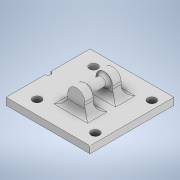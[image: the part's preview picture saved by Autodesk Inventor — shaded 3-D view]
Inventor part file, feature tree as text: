
AUTODESK INVENTOR PART (.ipt)
format: ipt  version: 2022 (Build 260153000, 153)  size: 207,360 bytes
history: native  units: in
note: dims shown in document units (in); Inventor stores cm internally (conversion verified against a paired STEP export)
features: sketch x6, extrude x4, fillet x3, hole x1
ambient origin geometry x8: Origin, YZ Plane, XZ Plane, XY Plane, X Axis, Y Axis, Z Axis, Center Point
bodies: Solid1 (feature_tree)
feature tree (14):
  extrude  "Extrusion1"  Depth=1.1811in
  hole  "Hole1"  [1 undecoded]
  extrude  "Extrusion2"  Depth=0.7953in
  extrude  "Extrusion3"  Depth=0.1929in
  fillet  "Fillet1"  Radius=0.7953in
  extrude  "Extrusion4"  Depth=0.0787in
  fillet  "Fillet2"  Radius=0.1929in
  fillet  "Fillet3"  Radius=0.1929in
  sketch  "Sketch6"  dims[d18=0.1181in d19=0.8189in d20=0.1929in d21=0.1929in d22=0.2362in d23=0.1181in d24=0.3346in d25=0.4094in d26=0.1181in d27=0.2756in d28=0.5354in d29=0.4094in d30=0.2756in d31=0.0in d32=0.1181in d33=0.1181in d34=0.1772in d35=0.1181in d36=0.1969in d37=0.0in d38=0.0394in d39=0.0787in]
  sketch  "Sketch1"  dims[d0=1.1811in d1=1.1811in]
  sketch  "Sketch2"  dims[d2=0.0984in d3=0.0in]
  sketch  "Sketch3"  dims[d4=0.1181in d5=0.2362in d6=0.1575in d7=0.0394in d8=90.0deg d9=0.315in d10=0.8108in d11=0.0787in]
  sketch  "Sketch4"  dims[d12=0.0394in d13=0.0in d14=0.7953in]
  sketch  "Sketch5"  dims[d15=0.8189in d16=0.1929in d17=0.7953in]
note: 1 required parameter value undecoded (feature->parameter linkage not recoverable at this tier; creation-order binding heuristic only, values carry confidence <= 0.55)
